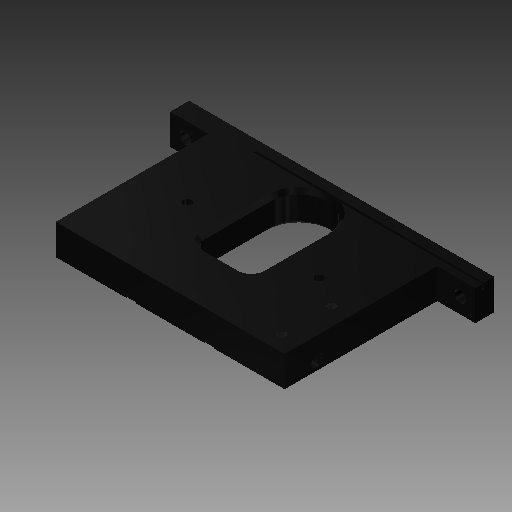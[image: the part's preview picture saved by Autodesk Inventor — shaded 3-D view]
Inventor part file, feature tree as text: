
AUTODESK INVENTOR PART (.ipt)
format: ipt  version: 2018 (Build 220112000, 112)  size: 355,840 bytes
history: native  units: mm
features: extrude x7, hole x5, mirror x3, other x3, projected_geometry x3, chamfer x2, sketch x2, fillet x1, reference x1
ambient origin geometry x8: Origin, YZ Plane, XZ Plane, XY Plane, X Axis, Y Axis, Z Axis, Center Point
bodies: Volumenkörper1 (feature_tree)
feature tree (27):
  extrude  "Extrusion1"  Depth=90.0mm
  extrude  "Extrusion2"  Depth=10.0mm
  extrude  "Extrusion3"  Depth=3.0mm TaperAngle=0.0deg
  chamfer  "Fase1"  Distance=30.0mm
  extrude  "Extrusion4"  Depth=10.0mm
  extrude  "Extrusion5"  Depth=15.0mm
  mirror  "Spiegeln1"
  chamfer  "Fase2"  Distance=3.0mm
  extrude  "Extrusion6"  Depth=6.5mm
  fillet  "Rundung1"  Radius=5.0mm
  hole  "Bohrung1"  [1 undecoded]
  extrude  "Extrusion7"  TaperAngle=90.0deg  [1 undecoded]
  hole  "Bohrung2"  [1 undecoded]
  mirror  "Spiegeln2"
  other  "Fläche verschieben1"
  other  "Fläche verschieben2"
  hole  "Bohrung3"  [1 undecoded]
  mirror  "Spiegeln3"
  hole  "Bohrung4"  [1 undecoded]
  other  "Fläche verschieben3"
  hole  "Bohrung5"  [1 undecoded]
  sketch  "Skizze7"  dims[d0=90.0mm d1=120.0mm]
  projected_geometry  "Projizierte Kontur1"
  projected_geometry  "Projizierte Kontur2"
  projected_geometry  "Projizierte Kontur3"
  sketch  "Skizze10"  dims[d2=30.0mm d3=0.0mm d4=1.2mm d6=3.0mm d7=0.0mm d8=30.0mm d9=55.0mm d10=15.0mm d13=3.0mm d14=0.0mm d17=6.5mm d18=5.0mm d19=15.0mm d20=90.0deg d21=90.0deg d22=62.5mm d23=16.0mm d24=60.0mm d25=2.0mm d26=2.0mm d27=45.0deg d28=4.0mm d29=3.0mm d30=15.0mm d31=25.0mm d32=0.0mm d33=3.0mm d34=18.0mm d35=23.0mm d36=5.0mm d37=67.5mm d38=14.0mm d39=0.0mm d40=2.0mm d41=2.0mm d42=45.0deg d43=5.0mm d44=0.0mm d45=2.0mm d46=4.5mm d47=8.0mm d48=6.5mm d49=7.5mm d50=6.0mm d51=6.0mm d52=4.0mm d53=2.0mm d54=90.0deg d55=8.0mm d56=20.594885mm d57=20.0mm d58=16.0mm d59=10.0mm d60=0.0mm d61=8.0mm d62=6.0mm d63=6.0mm d64=4.0mm d65=2.0mm d66=90.0deg d67=8.0mm d68=20.594885mm d69=11.5mm d70=46.5mm d71=4.4mm d72=6.0mm d73=4.0mm d74=2.0mm d75=90.0deg d76=8.0mm d77=20.594885mm d78=9.5mm d79=9.5mm d80=8.0mm d81=34.0mm d82=4.134mm d83=6.0mm d84=4.0mm d85=2.0mm d86=90.0deg d87=8.0mm d88=20.594885mm d89=40.0mm d90=40.0mm d91=2.5mm d92=2.5mm d93=2.459mm d94=8.0mm d95=4.0mm d96=2.0mm d97=90.0deg d98=10.0mm d99=20.594885mm]
  reference  "Referenz1"
note: 6 required parameter values undecoded (feature->parameter linkage not recoverable at this tier; creation-order binding heuristic only, values carry confidence <= 0.55)
